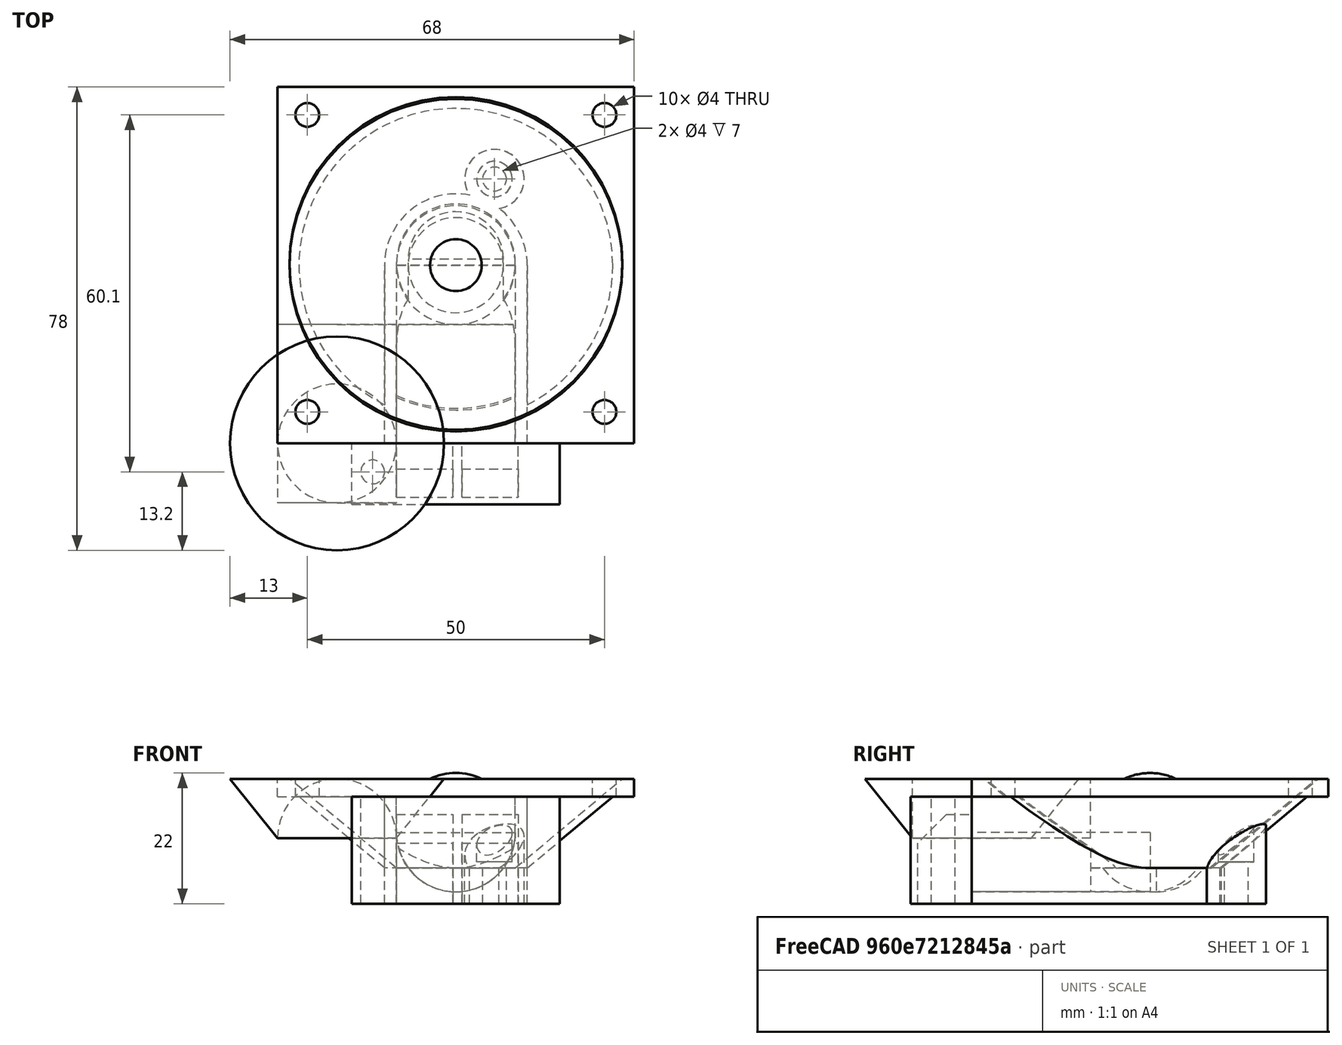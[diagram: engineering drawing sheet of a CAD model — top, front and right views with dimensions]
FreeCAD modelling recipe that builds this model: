
FCSTD DOCUMENT  (FreeCAD 0.16R6712 (Git))
Label: E3DV6_6060FanDuct
License: All rights reserved
LicenseURL: http://en.wikipedia.org/wiki/All_rights_reserved
objects: Part::MultiFuse×12, Part::Cylinder×12, Part::Box×8, Part::Feature×5, Part::Cone×4, Part::Cut×3, Part::Sphere×2
note: 46 computed .brp shape members not serialized (recipe doc carries the construction recipe); baked Part::Feature solids carry a one-line shape summary decoded from their .brp

FEATURE [Part::Box] Box  label="Würfel"
  Height = 3
  Length = 60
  Placement = pos=(-10,0,7) rot=(0,0,1;0rad)
  Width = 60
FEATURE [Part::Cone] Cone  label="Kegel"
  Angle = 360
  Height = 15
  Placement = pos=(20,30,-5) rot=(0,0,1;0rad)
  Radius1 = 10
  Radius2 = 28
FEATURE [Part::Cone] Cone001  label="Kegel001"
  Angle = 360
  Height = 15
  Placement = pos=(20,30,-5) rot=(0,0,1;0rad)
  Radius1 = 12
  Radius2 = 30
FEATURE [Part::Box] Box001  label="Würfel001"
  Height = 18
  Length = 35
  Placement = pos=(2.5,-10,-11) rot=(0,0,1;0rad)
  Width = 10.3
FEATURE [Part::MultiFuse] Fusion  label="PlatteAussenTrichter"
  Shapes = -> [Cone001,Box]
FEATURE [Part::Box] Box002  label="Würfel002"
  Height = 6
  Length = 20
  Placement = pos=(10,-10,1) rot=(0,0,1;0rad)
  Width = 30
FEATURE [Part::Box] Box003  label="Würfel003"
  Height = 18
  Length = 24
  Placement = pos=(8,-10,-11) rot=(0,0,1;0rad)
  Width = 30
FEATURE [Part::Cylinder] Cylinder001  label="Zylinder001"
  Angle = 360
  Height = 12
  Placement = pos=(20,20,-11) rot=(0,0,1;0rad)
  Radius = 12
FEATURE [Part::MultiFuse] Fusion003  label="aussen"
  Placement = pos=(0,10,0) rot=(0,0,1;0rad)
  Shapes = -> [Box003,Cylinder001]
FEATURE [Part::Cone] Cone002  label="Kegel002"
  Angle = 360
  Height = 10
  Radius1 = 10
  Radius2 = 18
FEATURE [Part::Sphere] Sphere  label="Kugel"
  Angle1 = -90
  Angle2 = 90
  Angle3 = 360
  Placement = pos=(20,20,1) rot=(1,0,0;0.017453rad)
  Radius = 10
FEATURE [Part::Cylinder] Cylinder002  label="Zylinder002"
  Angle = 180
  Height = 30
  Placement = pos=(0,20,0) rot=(1,0,0;1.5708rad)
  Radius = 10
FEATURE [Part::Feature] Cylinder003  label="Zylinder003"
  Placement = pos=(20,-10,1) rot=(0,1,0;3.14159rad)
  shape: bbox 20 x 20 x 10 mm, 4 faces (baked)
FEATURE [Part::MultiFuse] Fusion004  label="inner"
  Placement = pos=(0,10,0) rot=(0,0,1;0rad)
  Shapes = -> [Cylinder003,Box002,Sphere]
FEATURE [Part::MultiFuse] Fusion005  label="Hohlraum__Obsolete"
  Shapes = -> [Cone,Fusion004]
FEATURE [Part::MultiFuse] Fusion006  label="Wall"
  Shapes = -> [Fusion,Fusion003]
FEATURE [Part::Box] Box004  label="Würfel004"
  Height = 15
  Length = 9.5
  Placement = pos=(10,-8.8,-11) rot=(0,0,1;0rad)
  Width = 10
FEATURE [Part::Box] Box006  label="Würfel006"
  Height = 15
  Length = 9.5
  Placement = pos=(21,-8.8,-11) rot=(0,0,1;0rad)
  Width = 10
FEATURE [Part::MultiFuse] Fusion007
  Shapes = -> [Box004,Box006]
FEATURE [Part::Cylinder] Cylinder004  label="Zylinder004"
  Angle = 360
  Height = 20
  Placement = pos=(6,-4.5,-12) rot=(0,0,1;0rad)
  Radius = 2
FEATURE [Part::Box] Box007  label="Würfel007"
  Height = 10
  Length = 36
  Placement = pos=(0,-10,-2) rot=(1,0,0;0.785398rad)
  Width = 10
FEATURE [Part::Cut] Cut001
  Base = -> Fusion007
  Tool = -> Box007
FEATURE [Part::Cylinder] Cylinder005  label="Zylinder005"
  Angle = 360
  Height = 10
  Radius = 2
FEATURE [Part::Cylinder] Cylinder006  label="Zylinder006"
  Angle = 360
  Height = 10
  Placement = pos=(0,50,0) rot=(0,0,1;0rad)
  Radius = 2
FEATURE [Part::Cylinder] Cylinder007  label="Zylinder007"
  Angle = 360
  Height = 10
  Placement = pos=(50,0,0) rot=(0,0,1;0rad)
  Radius = 2
FEATURE [Part::Cylinder] Cylinder008  label="Zylinder008"
  Angle = 360
  Height = 10
  Placement = pos=(50,50,0) rot=(0,0,1;0rad)
  Radius = 2
FEATURE [Part::MultiFuse] Fusion008  label="LüfterBohrung"
  Placement = pos=(-5,5.3,2) rot=(0,0,1;0rad)
  Shapes = -> [Cylinder005,Cylinder006,Cylinder008,Cylinder007]
FEATURE [Part::Feature] Cylinder002001  label="Zylinder009"
  Placement = pos=(20,10,1) rot=(0,1,0;3.14159rad)
  shape: bbox 20 x 30 x 10 mm, 4 faces (baked)
FEATURE [Part::Cylinder] Cylinder002002  label="HalterObenVoll"
  Angle = 360
  Height = 15
  Placement = pos=(26.5,44.5,-11) rot=(0,0,1;0rad)
  Radius = 5
FEATURE [Part::Cylinder] Cylinder002003  label="HalteBohrungOben"
  Angle = 360
  Height = 30
  Placement = pos=(26.5,44.5,-13) rot=(0,0,1;0rad)
  Radius = 2
FEATURE [Part::Cone] Cone003  label="SchnittKegel"
  Angle = 360
  Height = 15
  Placement = pos=(20,30.3,-5) rot=(0,0,1;0rad)
  Radius1 = 10
  Radius2 = 28
FEATURE [Part::Cylinder] Cylinder002004  label="HalteSenkeOben"
  Angle = 360
  Height = 11
  Placement = pos=(26.5,44.5,-4) rot=(0,0,1;0rad)
  Radius = 3
FEATURE [Part::Box] Box008  label="Würfel008"
  Height = 6
  Length = 20
  Placement = pos=(10,-11,1) rot=(0,0,1;0rad)
  Width = 31
FEATURE [Part::Sphere] Sphere001  label="Kugel001"
  Angle1 = -90
  Angle2 = 90
  Angle3 = 360
  Placement = pos=(20,20,1) rot=(1,0,0;0.017453rad)
  Radius = 10
FEATURE [Part::Cylinder] Cylinder  label="Zylinder"
  Angle = 180
  Height = 31
  Placement = pos=(20,-11,1) rot=(-1,0,0;1.5708rad)
  Radius = 10
FEATURE [Part::Cylinder] Cylinder002006  label="Zylinder014"
  Angle = 360
  Height = 6
  Placement = pos=(20,20,1) rot=(0,0,1;0rad)
  Radius = 10
FEATURE [Part::MultiFuse] Fusion011  label="LuftSchacht"
  Placement = pos=(0,11,0) rot=(0,0,1;0rad)
  Shapes = -> [Box008,Cylinder,Cylinder002006,Sphere001]
FEATURE [Part::MultiFuse] Fusion012  label="Hohlraum"
  Shapes = -> [Fusion008,Cylinder002003,Cone003,Cylinder002004,Fusion011]
FEATURE [Part::MultiFuse] Fusion013  label="FanDuctVoll"
  Shapes = -> [Cylinder002002,Fusion006]
FEATURE [Part::Cut] Cut  label="FanDuct"
  Base = -> Fusion013
  Tool = -> Fusion012
FEATURE [Part::MultiFuse] Fusion014
  Shapes = -> [Cut001,Cylinder004]
FEATURE [Part::Cut] Cut002
  Base = -> Box001
  Placement = pos=(0,-0.3,0) rot=(0,0,1;0rad)
  Tool = -> Fusion014
FEATURE [Part::Feature] Cut002_solid  label="Cut002 (Solid)"
  shape: bbox 35 x 10.3 x 18 mm, 17 faces (baked)
FEATURE [Part::Feature] Cut_solid  label="FanDuct (Solid)"
  shape: bbox 60 x 60 x 21 mm, 38 faces (baked)
FEATURE [Part::MultiFuse] Fusion015
  Shapes = -> [Cut002_solid,Cut_solid]
FEATURE [Part::Feature] Fusion015001  label="Fusion016"
  shape: bbox 60 x 70.3 x 21 mm, 45 faces (baked)
